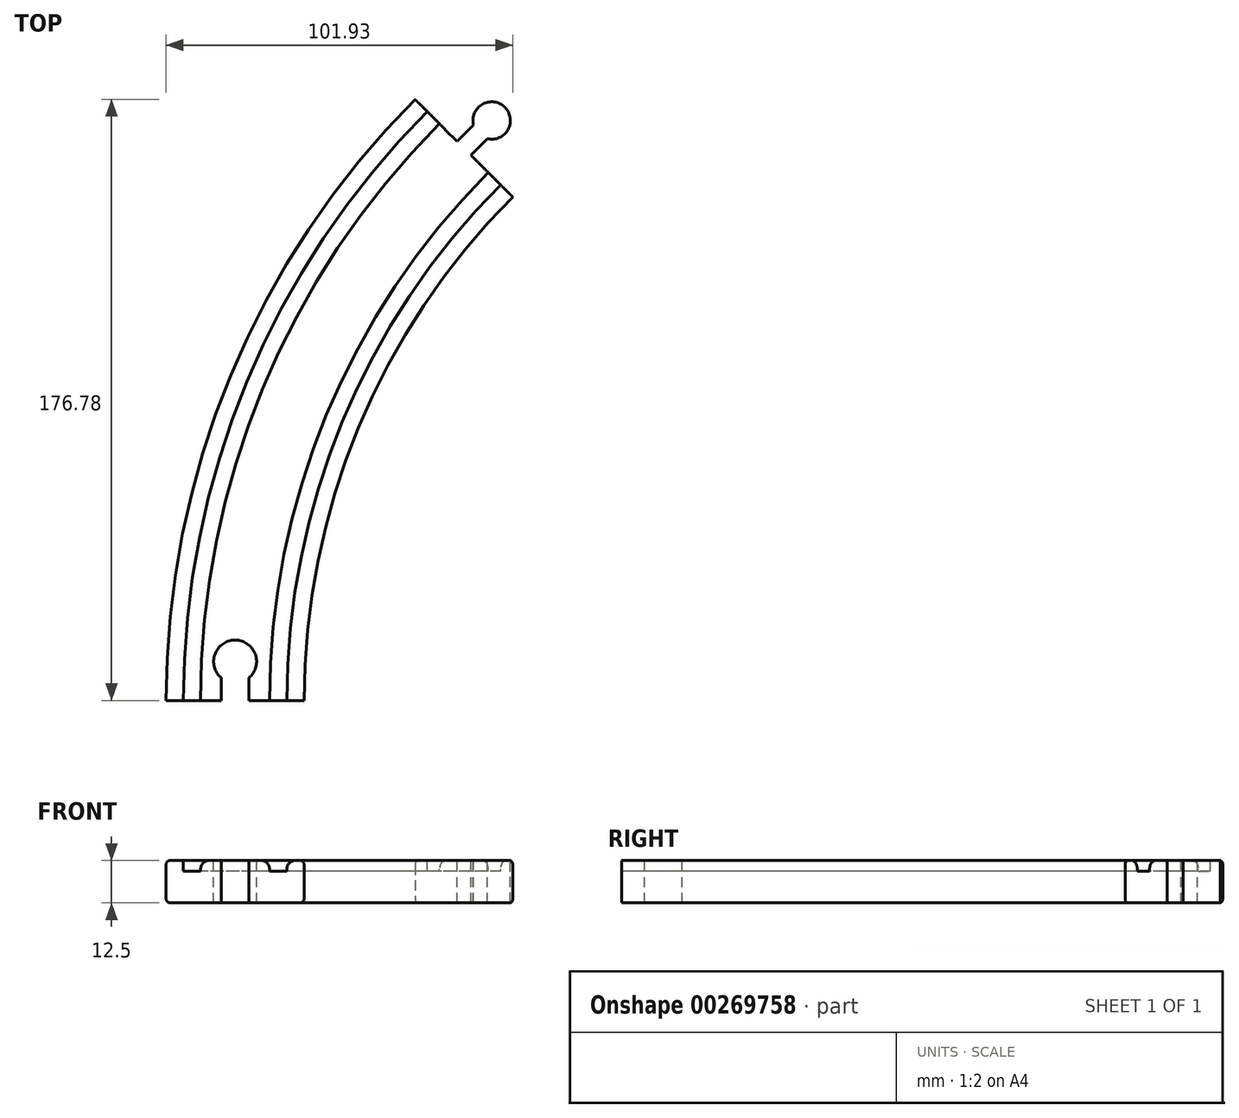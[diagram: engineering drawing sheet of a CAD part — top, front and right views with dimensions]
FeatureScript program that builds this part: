
annotation { "Feature Type Name" : "Feature", "Feature Type Description" : "" }
export const myFeature = defineFeature(function(context is Context, id is Id, definition is map)
    precondition{}
    {
        {
            var Q0;
            Q0=qCreatedBy(makeId("Top.planeOp"),FACE);
            var sketch = newSketch(context, id + "F0", { "sketchPlane" : qUnion([Q0])});
            skArc(sketch, "E0", {"start": v(-176.78, 176.78) * mm, "mid": v(-230.97, 95.67) * mm, "end": v(-250, 0) * mm});
            skArc(sketch, "E1", {"start": v(-148.07, 148.07) * mm, "mid": v(-193.46, 80.13) * mm, "end": v(-209.4, 0) * mm});
            skLineSegment(sketch, "E2", {"start": v(-209.4, 0) * mm, "end": v(-250, 0) * mm});
            skLineSegment(sketch, "E3", {"start": v(-148.07, 148.07) * mm, "end": v(-176.78, 176.78) * mm});
            skSolve(sketch);
        }
        {
            var Q0;
            Q0 = qSketchRegion(id + "F0", true);
            extrude(context, id + "F1", {"entities" : qUnion([Q0]), "depth" : 12.5 * mm});
        }
        {
            var Q0;
            Q0=makeQuery(id+"F1.opExtrude","CAP_FACE",FACE,{"disambiguationData":[OSD([sQuery(id+"F0.wireOp",EDGE,"E0"),sQuery(id+"F0.wireOp",EDGE,"E1"),sQuery(id+"F0.wireOp",EDGE,"E2"),sQuery(id+"F0.wireOp",EDGE,"E3")])],"isStart":false});
            var sketch = newSketch(context, id + "F2", { "sketchPlane" : qUnion([Q0])});
            skLineSegment(sketch, "E4", {"start": v(-229.7, 0) * mm, "end": v(-229.7, 11.48) * mm, "construction": true});
            skArc(sketch, "E5", {"start": v(-225.6, 6.7) * mm, "mid": v(-229.7, 17.78) * mm, "end": v(-233.8, 6.7) * mm});
            skLineSegment(sketch, "E6", {"start": v(-229.7, 0) * mm, "end": v(-233.8, 0) * mm});
            skLineSegment(sketch, "E7", {"start": v(-233.8, 0) * mm, "end": v(-233.8, 6.7) * mm});
            skLineSegment(sketch, "E8", {"start": v(-229.7, 0) * mm, "end": v(-225.6, 0) * mm});
            skLineSegment(sketch, "E9", {"start": v(-225.6, 0) * mm, "end": v(-225.6, 6.7) * mm});
            skSolve(sketch);
        }
        {
            var Q0;
            Q0 = qSketchRegion(id + "F2", true);
            extrude(context, id + "F3", {"entities" : qUnion([Q0]), "operationType" : NewBodyOperationType.REMOVE, "endBound" : BoundingType.THROUGH_ALL, "oppositeDirection" : true, "depth" : 25 * mm});
        }
        {
            var Q0;
            Q0=makeQuery(id+"F1.opExtrude","CAP_FACE",FACE,{"disambiguationData":[OSD([sQuery(id+"F0.wireOp",EDGE,"E0"),sQuery(id+"F0.wireOp",EDGE,"E1"),sQuery(id+"F0.wireOp",EDGE,"E2"),sQuery(id+"F0.wireOp",EDGE,"E3")])],"isStart":false});
            var sketch = newSketch(context, id + "F4", { "sketchPlane" : qUnion([Q0])});
            skArc(sketch, "E10.0", {"start": v(-173.18, 173.18) * mm, "mid": v(-226.28, 93.73) * mm, "end": v(-244.92, 0) * mm});
            skArc(sketch, "E11.0", {"start": v(-169.6, 169.6) * mm, "mid": v(-221.58, 91.78) * mm, "end": v(-239.84, 0) * mm});
            skLineSegment(sketch, "E12", {"start": v(-173.18, 173.18) * mm, "end": v(-169.6, 169.6) * mm});
            skLineSegment(sketch, "E13", {"start": v(-244.92, 0) * mm, "end": v(-239.84, 0) * mm});
            skArc(sketch, "E14.0", {"start": v(-151.66, 151.66) * mm, "mid": v(-198.15, 82.08) * mm, "end": v(-214.48, 0) * mm});
            skArc(sketch, "E15.0", {"start": v(-155.25, 155.25) * mm, "mid": v(-202.85, 84.02) * mm, "end": v(-219.56, 0) * mm});
            skLineSegment(sketch, "E16", {"start": v(-155.25, 155.25) * mm, "end": v(-151.66, 151.66) * mm});
            skLineSegment(sketch, "E17", {"start": v(-219.56, 0) * mm, "end": v(-214.48, 0) * mm});
            skSolve(sketch);
        }
        {
            var Q0;
            Q0 = qSketchRegion(id + "F4", true);
            extrude(context, id + "F5", {"entities" : qUnion([Q0]), "operationType" : NewBodyOperationType.REMOVE, "oppositeDirection" : true, "depth" : 3.17 * mm});
        }
        {
            var Q0;
            Q0=makeQuery(id+"F1.opExtrude","SWEPT_EDGE",EDGE,{"disambiguationData":[OSD([sQuery(id+"F0.wireOp",EDGE,"E1"),sQuery(id+"F0.wireOp",EDGE,"E2")])]});
            cPlane(context, id + "F6", {"entities" : qUnion([Q0]), "cplaneType" : CPlaneType.MID_PLANE, "offset" : 25 * mm, "width" : 150 * mm, "height" : 150 * mm});
        }
        {
            var Q0;
            Q0=makeQuery(id+"F1.opExtrude","CAP_EDGE",EDGE,{"disambiguationData":[OSD([sQuery(id+"F0.wireOp",EDGE,"E0")])],"isStart":false});
            var Q1;
            Q1=makeQuery(id+"F1.opExtrude","CAP_EDGE",EDGE,{"disambiguationData":[OSD([sQuery(id+"F0.wireOp",EDGE,"E1")])],"isStart":false});
            var Q2;
            Q2=makeQuery(id+"F1.opExtrude","CAP_EDGE",EDGE,{"disambiguationData":[OSD([sQuery(id+"F0.wireOp",EDGE,"E1")])],"isStart":true});
            var Q3;
            Q3=makeQuery(id+"F1.opExtrude","CAP_EDGE",EDGE,{"disambiguationData":[OSD([sQuery(id+"F0.wireOp",EDGE,"E0")])],"isStart":true});
            fillet(context, id + "F7", {"entities" : qUnion([Q0, Q1, Q2, Q3]), "radius" : 1.27 * mm, "tangentPropagation" : true, "allowEdgeOverflow" : false});
        }
        {
            var Q0;
            Q0=makeQuery(id+"F5.boolean.opBoolean","COPY",EDGE,{"derivedFrom":makeQuery(id+"F5.opExtrude","CAP_EDGE",EDGE,{"disambiguationData":[OSD([sQuery(id+"F4.wireOp",EDGE,"E10.0")])],"isStart":true})});
            var Q1;
            Q1=makeQuery(id+"F5.boolean.opBoolean","COPY",EDGE,{"derivedFrom":makeQuery(id+"F5.opExtrude","CAP_EDGE",EDGE,{"disambiguationData":[OSD([sQuery(id+"F4.wireOp",EDGE,"E14.0")])],"isStart":true})});
            var Q2;
            Q2=makeQuery(id+"F5.boolean.opBoolean","COPY",EDGE,{"derivedFrom":makeQuery(id+"F5.opExtrude","CAP_EDGE",EDGE,{"disambiguationData":[OSD([sQuery(id+"F4.wireOp",EDGE,"E11.0")])],"isStart":true})});
            var Q3;
            Q3=makeQuery(id+"F5.boolean.opBoolean","COPY",EDGE,{"derivedFrom":makeQuery(id+"F5.opExtrude","CAP_EDGE",EDGE,{"disambiguationData":[OSD([sQuery(id+"F4.wireOp",EDGE,"E15.0")])],"isStart":true})});
            var Q4;
            Q4=makeQuery(id+"FlMNfWnsh4HgeSK_1.1.F5.boolean.opBoolean","COPY",EDGE,{"derivedFrom":makeQuery(id+"FlMNfWnsh4HgeSK_1.1.F5.opExtrude","CAP_EDGE",EDGE,{"disambiguationData":[OSD([sQuery(id+"F4.wireOp",EDGE,"E11.0")])],"isStart":true})});
            var Q5;
            Q5=makeQuery(id+"FlMNfWnsh4HgeSK_1.1.F5.boolean.opBoolean","COPY",EDGE,{"derivedFrom":makeQuery(id+"FlMNfWnsh4HgeSK_1.1.F5.opExtrude","CAP_EDGE",EDGE,{"disambiguationData":[OSD([sQuery(id+"F4.wireOp",EDGE,"E10.0")])],"isStart":true})});
            var Q6;
            Q6=makeQuery(id+"FlMNfWnsh4HgeSK_1.1.F5.boolean.opBoolean","COPY",EDGE,{"derivedFrom":makeQuery(id+"FlMNfWnsh4HgeSK_1.1.F5.opExtrude","CAP_EDGE",EDGE,{"disambiguationData":[OSD([sQuery(id+"F4.wireOp",EDGE,"E14.0")])],"isStart":true})});
            var Q7;
            Q7=makeQuery(id+"FlMNfWnsh4HgeSK_1.1.F5.boolean.opBoolean","COPY",EDGE,{"derivedFrom":makeQuery(id+"FlMNfWnsh4HgeSK_1.1.F5.opExtrude","CAP_EDGE",EDGE,{"disambiguationData":[OSD([sQuery(id+"F4.wireOp",EDGE,"E15.0")])],"isStart":true})});
            fillet(context, id + "F8", {"entities" : qUnion([Q0, Q1, Q2, Q3, Q4, Q5, Q6, Q7]), "radius" : 2.54 * mm, "tangentPropagation" : true, "allowEdgeOverflow" : false});
        }
        {
            var Q0;
            {var subQ0=sQuery(id+"F0.wireOp",EDGE,"E3");var subQ1=sQuery(id+"F0.wireOp",EDGE,"E2");Q0=makeQuery(id+"F5.boolean.opBoolean","SPLIT",FACE,{"disambiguationData":[TD([makeQuery(id+"F3.boolean.opBoolean","COPY",FACE,{"derivedFrom":makeQuery(id+"F3.opExtrude","SWEPT_FACE",FACE,{"disambiguationData":[OSD([sQuery(id+"F2.wireOp",EDGE,"E5")])]})})])],"derivedFrom":makeQuery(id+"F1.opExtrude","CAP_FACE",FACE,{"disambiguationData":[OSD([sQuery(id+"F0.wireOp",EDGE,"E0"),sQuery(id+"F0.wireOp",EDGE,"E1"),subQ1,subQ0])],"isStart":false})});}
            var sketch = newSketch(context, id + "F9", { "sketchPlane" : qUnion([Q0])});
            skLineSegment(sketch, "E18", {"start": v(-162.42, 162.42) * mm, "end": v(-154.26, 170.59) * mm, "construction": true});
            skCircle(sketch, "E19", {"center": v(-154.26, 170.59) * mm, "radius": 5.5 * mm});
            skLineSegment(sketch, "E20", {"start": v(-162.42, 162.42) * mm, "end": v(-160.39, 160.39) * mm});
            skLineSegment(sketch, "E21", {"start": v(-160.39, 160.39) * mm, "end": v(-155.54, 165.24) * mm});
            skLineSegment(sketch, "E22", {"start": v(-162.42, 162.42) * mm, "end": v(-164.46, 164.46) * mm});
            skLineSegment(sketch, "E23", {"start": v(-164.46, 164.46) * mm, "end": v(-159.6, 169.3) * mm});
            skSolve(sketch);
        }
        {
            var Q0;
            Q0 = qSketchRegion(id + "F9", true);
            var Q1;
            {var subQ0=sQuery(id+"F0.wireOp",EDGE,"E3");var subQ1=sQuery(id+"F0.wireOp",EDGE,"E2");Q1=makeQuery(id+"FgHu2bbrGD5gaZU_1.1.F5.boolean.opBoolean","SPLIT",FACE,{"disambiguationData":[TD([makeQuery(id+"F3.boolean.opBoolean","COPY",FACE,{"derivedFrom":makeQuery(id+"F3.opExtrude","SWEPT_FACE",FACE,{"disambiguationData":[OSD([sQuery(id+"F2.wireOp",EDGE,"E5")])]})})])],"derivedFrom":makeQuery(id+"F1.opExtrude","CAP_FACE",FACE,{"disambiguationData":[OSD([sQuery(id+"F0.wireOp",EDGE,"E0"),sQuery(id+"F0.wireOp",EDGE,"E1"),subQ1,subQ0])],"isStart":true})});}
            extrude(context, id + "F10", {"entities" : qUnion([Q0]), "operationType" : NewBodyOperationType.ADD, "endBound" : BoundingType.UP_TO_SURFACE, "oppositeDirection" : true, "endBoundEntityFace" : qUnion([Q1]), "depth" : 25 * mm});
        }
    });
